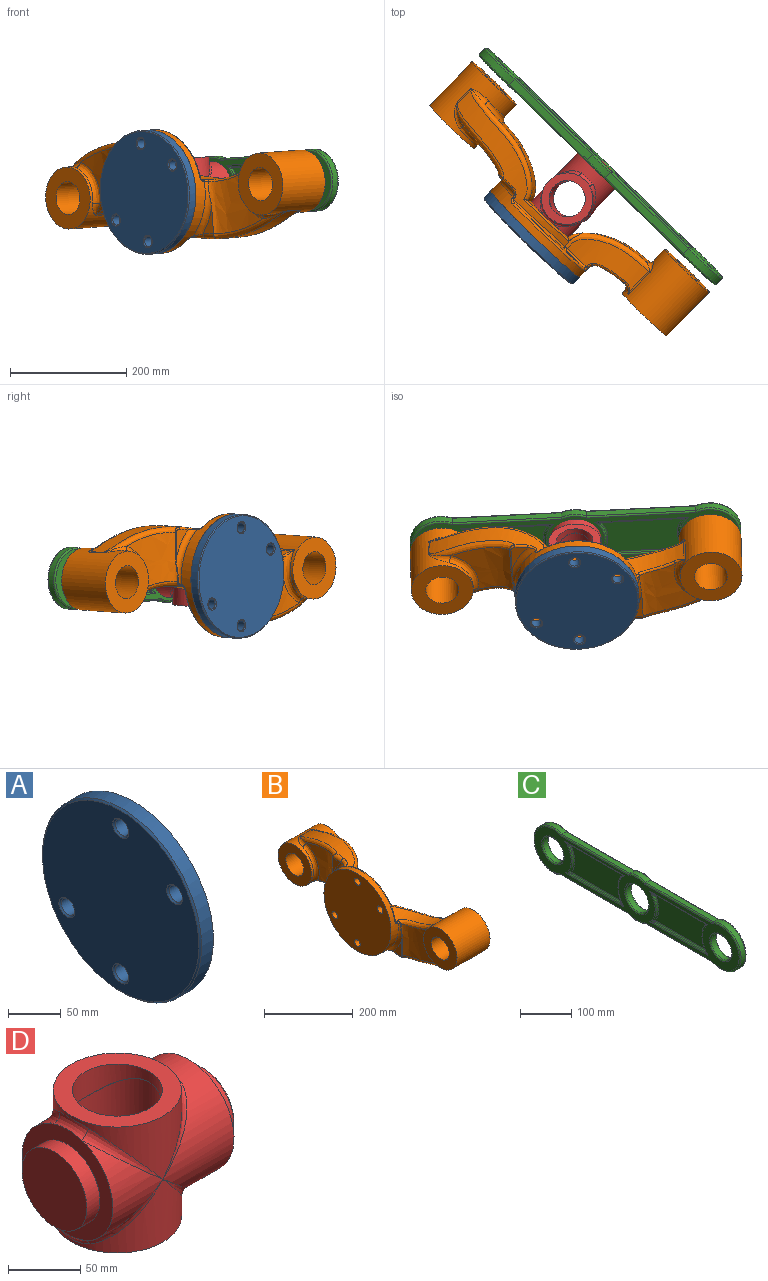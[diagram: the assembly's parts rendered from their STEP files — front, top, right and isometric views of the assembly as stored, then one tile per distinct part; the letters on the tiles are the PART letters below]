
ASSEMBLY  parts=4 mates=4
PART A: 12 faces, bbox 17.8x213.4x213.4 mm
  f0: cylinder r=8.89mm len=17.78mm, axis (1,0,0), area 893.8mm2, adj f6,f9
  f1: cylinder r=106.68mm len=213.36mm, axis (1,0,0), area 10726mm2, adj f6,f11
  f2: cylinder r=8.89mm len=17.78mm, axis (1,0,0), area 893.8mm2, adj f6,f10
  f3: cylinder r=8.89mm len=17.78mm, axis (1,0,0), area 893.8mm2, adj f6,f7
  f4: cylinder r=8.89mm len=17.78mm, axis (1,0,0), area 893.8mm2, adj f6,f8
  f5: plane 209.8x209.8mm, normal (-1,0,0), area 33141.3mm2, adj f7,f8,f9,f10,f11
  f6: plane 213.36x213.36mm, normal (1,0,0), area 34760.1mm2, adj f0,f1,f2,f3,f4
  f7: cone r=10.67mm half-angle=45deg, axis (-1,0,0), area 154.5mm2, adj f3,f5
  f8: cone r=10.67mm half-angle=45deg, axis (-1,0,0), area 154.5mm2, adj f4,f5
  f9: cone r=10.67mm half-angle=45deg, axis (-1,0,0), area 154.5mm2, adj f0,f5
  f10: cone r=8.89mm half-angle=45deg, axis (-1,0,0), area 154.5mm2, adj f2,f5
  f11: cone r=104.9mm half-angle=45deg, axis (1,0,0), area 1671.4mm2, adj f1,f5
PART B: 101 faces, bbox 139.1x569.9x231.1 mm
  f0: plane 151.16x93.4mm, normal (1,0,0), area 3907.4mm2, adj f7,f12,f25,f38,f78,f79,f80,f81
  f1: plane 106.68x106.68mm, normal (1,0,0), area 6395.9mm2, adj f2,f3
  f2: cylinder r=28.45mm len=104.9mm, axis (-1,0,0), area 18750.6mm2, adj f1,f4
  f3: cylinder r=53.34mm len=106.68mm, axis (-1,0,0), area 26347mm2, adj f1,f4,f40,f43,f44,f46,f47,f48
  f4: plane 106.68x106.68mm, normal (-1,0,0), area 6395.9mm2, adj f2,f3
  f5: cylinder r=256.25mm len=304.31mm, axis (-1,0,0), area 8276mm2, adj f25,f31,f32,f42,f58,f61,f62,f63
  f6: cylinder r=153.13mm len=128.87mm, axis (-1,0,0), area 4941.8mm2, adj f23,f29,f30,f67
  f7: extruded ~167.29x103.82mm, area 14672.5mm2, adj f0,f23,f24,f25,f78
  f8: extruded ~104.19x93.39mm, area 6218.3mm2, adj f29,f32,f35,f65,f66
  f9: cylinder r=256.25mm len=304.31mm, axis (-1,0,0), area 8055.6mm2, adj f23,f36,f38,f39,f41,f44,f45,f74
  f10: cylinder r=153.13mm len=128.87mm, axis (-1,0,0), area 5509.7mm2, adj f42,f48,f51,f52,f53,f54,f55
  f11: extruded ~104.21x99.66mm, area 7531.8mm2, adj f15,f37,f45,f49,f52
  f12: extruded ~167.29x103.82mm, area 14672.6mm2, adj f0,f38,f42,f43,f80
  f13: cylinder r=106.68mm len=213.36mm, axis (-1,0,0), area 11463.9mm2, adj f22,f26,f36,f37,f55,f57,f59,f60
  f14: plane 46.65x28.37mm, normal (-1,0,0), area 555.7mm2, adj f26,f63,f64,f65
  f15: plane 46.02x25.19mm, normal (-1,0,0), area 488.5mm2, adj f11,f37,f41,f45
  f16: cylinder r=53.34mm len=106.68mm, axis (-1,0,0), area 26286.9mm2, adj f17,f19,f24,f27,f28,f30,f31,f33
  f17: plane 106.68x106.68mm, normal (1,0,0), area 6395.9mm2, adj f16,f18
  f18: cylinder r=28.45mm len=104.9mm, axis (-1,0,0), area 18750.6mm2, adj f17,f19
  f19: plane 106.68x106.68mm, normal (-1,0,0), area 6395.9mm2, adj f16,f18
  f20: plane 158.94x84.9mm, normal (1,0,0), area 5064.9mm2, adj f54,f56,f58,f59,f86,f87
  f21: plane 158.94x84.9mm, normal (1,0,0), area 5064.9mm2, adj f67,f70,f71,f74,f77,f88,f89
  f22: plane 213.36x213.36mm, normal (-1,0,0), area 34760.1mm2, adj f13,f82,f83,f84,f85
  f23: bspline ~154.44x103.07mm, area 2156.6mm2, adj f6,f7,f9,f27,f70,f78
  f24: bspline ~80.73x49.33mm, area 1147.9mm2, adj f7,f16,f27,f28
  f25: bspline ~206.66x83.42mm, area 2956.7mm2, adj f0,f5,f7,f28,f81
  f26: torus R=115.57mm, axis (1,0,0), area 1170.8mm2, adj f13,f14,f62,f66,f68
  f27: bspline ~24.63x19.85mm, area 221.3mm2, adj f16,f23,f24,f30
  f28: bspline ~41.59x10.05mm, area 287.6mm2, adj f16,f24,f25,f31
  f29: bspline ~96.96x42.4mm, area 1170.7mm2, adj f6,f8,f33,f68,f71,f72
  f30: cylinder r=8.89mm len=34mm, axis (1,0,0), area 127.3mm2, adj f6,f16,f27,f33
  f31: cylinder r=8.89mm len=29.85mm, axis (-1,0,0), area 43.7mm2, adj f5,f16,f28,f34
  f32: bspline ~154.3x46.45mm, area 1853mm2, adj f5,f8,f34,f64
  f33: bspline ~25.18x21.29mm, area 258.9mm2, adj f16,f29,f30,f35
  f34: bspline ~40.91x32.76mm, area 353.1mm2, adj f16,f31,f32,f35
  f35: bspline ~79.04x51.99mm, area 1244mm2, adj f8,f16,f33,f34
  f36: cylinder r=8.89mm len=7.64mm, axis (1,0,0), area 14.5mm2, adj f9,f13,f39,f69
  f37: torus R=115.57mm, axis (1,0,0), area 1174.3mm2, adj f11,f13,f15,f39,f52,f53
  f38: bspline ~208.41x102.25mm, area 2956.9mm2, adj f0,f9,f12,f40,f79
  f39: bspline ~25.71x19.57mm, area 262.5mm2, adj f9,f36,f37,f41
  f40: bspline ~41.59x10.05mm, area 287.6mm2, adj f3,f38,f43,f44
  f41: torus R=247.36mm, axis (1,0,0), area 337.2mm2, adj f9,f15,f39,f45
  f42: bspline ~151.03x88.51mm, area 2157mm2, adj f5,f10,f12,f46,f56,f80
  f43: bspline ~78.14x49.61mm, area 1148mm2, adj f3,f12,f40,f46
  f44: cylinder r=8.89mm len=29.85mm, axis (-1,0,0), area 43.7mm2, adj f3,f9,f40,f47
  f45: bspline ~152.31x46.35mm, area 1821.1mm2, adj f9,f11,f15,f41,f47
  f46: bspline ~24.63x19.85mm, area 221.3mm2, adj f3,f42,f43,f48
  f47: bspline ~40.91x32.76mm, area 353.1mm2, adj f3,f44,f45,f49
  f48: cylinder r=8.89mm len=52.38mm, axis (1,0,0), area 186.1mm2, adj f3,f10,f46,f50
  f49: bspline ~100.99x50.99mm, area 1476.1mm2, adj f3,f11,f47,f50,f51
  f50: bspline ~5.35x3.86mm, area 5.1mm2, adj f48,f49,f51
  f51: bspline ~18.89x11.72mm, area 75.4mm2, adj f10,f49,f50,f52
  f52: bspline ~72.74x21.99mm, area 382.9mm2, adj f10,f11,f37,f51,f53
  f53: bspline ~11.85x6.97mm, area 42mm2, adj f10,f37,f52,f55
  f54: torus R=149.57mm, axis (-1,0,0), area 251.8mm2, adj f10,f20,f56,f57
  f55: cylinder r=3.56mm len=3.21mm, axis (-1,0,0), area 8.7mm2, adj f10,f13,f53,f57
  f56: torus R=12.45mm, axis (-1,0,0), area 31.3mm2, adj f20,f42,f54,f58
  f57: bspline ~8.68x8.6mm, area 41.5mm2, adj f13,f54,f55,f59
  f58: torus R=259.81mm, axis (-1,0,0), area 717.3mm2, adj f5,f20,f56,f60
  f59: torus R=103.12mm, axis (-1,0,0), area 1167.9mm2, adj f13,f20,f57,f60
  f60: bspline ~11x7.79mm, area 44.1mm2, adj f13,f58,f59,f61
  f61: cylinder r=3.56mm len=2.95mm, axis (1,0,0), area 5.6mm2, adj f5,f13,f60,f62
  f62: bspline ~16.84x14.77mm, area 82mm2, adj f5,f26,f61,f63
  f63: torus R=252.69mm, axis (1,0,0), area 119.6mm2, adj f5,f14,f62,f64
  f64: bspline ~12.14x10.45mm, area 48.7mm2, adj f14,f32,f63,f65
  f65: cylinder r=3.56mm len=41.47mm, axis (0,0,1), area 105.9mm2, adj f8,f14,f64,f66
  f66: bspline ~52.44x4.31mm, area 66.1mm2, adj f8,f26,f65,f68
  f67: torus R=149.57mm, axis (-1,0,0), area 245.4mm2, adj f6,f21,f70,f71
  f68: bspline ~8.07x7.71mm, area 26.8mm2, adj f26,f29,f66,f72
  f69: torus R=12.45mm, axis (-1,0,0), area 14.5mm2, adj f36,f73,f74
  f70: torus R=12.45mm, axis (-1,0,0), area 31.3mm2, adj f21,f23,f67,f74
  f71: bspline ~6.66x4.9mm, area 12.1mm2, adj f21,f29,f67,f75
  f72: bspline ~8.91x2.8mm, area 5.9mm2, adj f13,f29,f68,f75
  f73: bspline ~8.94x6.4mm, area 12.7mm2, adj f13,f69,f76
  f74: torus R=259.81mm, axis (-1,0,0), area 716.1mm2, adj f9,f21,f69,f70,f76
  f75: bspline ~8.92x8.52mm, area 39.3mm2, adj f13,f71,f72,f77
  f76: bspline ~8.96x5.35mm, area 23.3mm2, adj f13,f73,f74,f77
  f77: torus R=103.12mm, axis (-1,0,0), area 1167.9mm2, adj f13,f21,f75,f76
  f78: bspline ~32.54x19.35mm, area 166.3mm2, adj f0,f7,f9,f23,f79
  f79: torus R=252.69mm, axis (-1,0,0), area 627.5mm2, adj f0,f9,f38,f78
  f80: bspline ~34.18x19.94mm, area 166.2mm2, adj f0,f5,f12,f42,f81
  f81: torus R=252.69mm, axis (-1,0,0), area 627.5mm2, adj f0,f5,f25,f80
  f82: cylinder r=8.89mm len=17.78mm, axis (1,0,0), area 893.8mm2, adj f22,f88
  f83: cylinder r=8.89mm len=17.78mm, axis (1,0,0), area 893.8mm2, adj f22,f89
  f84: cylinder r=8.89mm len=17.78mm, axis (1,0,0), area 893.8mm2, adj f22,f86
  f85: cylinder r=8.89mm len=17.78mm, axis (1,0,0), area 893.8mm2, adj f22,f87
  f86: cone r=8.89mm half-angle=45deg, axis (1,0,0), area 154.5mm2, adj f20,f84
  f87: cone r=8.89mm half-angle=45deg, axis (1,0,0), area 154.5mm2, adj f20,f85
  f88: cone r=8.89mm half-angle=45deg, axis (1,0,0), area 154.5mm2, adj f21,f82
  f89: cone r=10.67mm half-angle=45deg, axis (1,0,0), area 154.5mm2, adj f21,f83
  f90: cylinder r=44.45mm len=84.3mm, axis (-1,0,0), area 11.6mm2, adj f0,f92,f97,f98
  f91: cylinder r=44.45mm len=84.3mm, axis (-1,0,0), area 11.6mm2, adj f0,f94,f95,f98
  f92: bspline ~0.3x0.21mm, area 0mm2, adj f0,f90,f93
  f93: bspline ~30.61x9.54mm, area 3.1mm2, adj f0,f92,f94,f98
  f94: bspline ~0.3x0.21mm, area 0mm2, adj f0,f91,f93
  f95: bspline ~0.3x0.21mm, area 0mm2, adj f0,f91,f96
  f96: bspline ~30.61x9.54mm, area 3.1mm2, adj f0,f95,f97,f98
  f97: bspline ~0.3x0.21mm, area 0mm2, adj f0,f90,f96
  f98: plane 88.9x88.9mm, normal (1,0,0), area 2513.3mm2, adj f90,f91,f93,f96,f99
  f99: cylinder r=34.29mm len=68.58mm, axis (1,0,0), area 2736.2mm2, adj f98,f100
  f100: plane 68.58x68.58mm, normal (1,0,0), area 3693.9mm2, adj f99
PART C: 103 faces, bbox 17.8x578.5x115.5 mm
  f0: plane 187.19x12.45mm, normal (0,0,-1), area 2329.8mm2, adj f1,f10,f21,f40
  f1: cylinder r=53.34mm len=106.68mm, axis (-1,0,0), area 2654.3mm2, adj f0,f2,f19,f38
  f2: plane 187.19x12.45mm, normal (0,0,1), area 2329.8mm2, adj f1,f3,f17,f36
  f3: cylinder r=53.34mm len=44.31mm, axis (-1,0,0), area 568.7mm2, adj f2,f4,f18,f37
  f4: plane 187.19x12.45mm, normal (0,0,1), area 2329.8mm2, adj f3,f5,f20,f39
  f5: cylinder r=53.34mm len=106.68mm, axis (-1,0,0), area 2654.3mm2, adj f4,f6,f22,f41
  f6: plane 187.19x12.45mm, normal (0,0,-1), area 2329.8mm2, adj f5,f10,f24,f43
  f7: cylinder r=28.45mm len=56.9mm, axis (-1,0,0), area 2224.6mm2, adj f29,f48
  f8: cylinder r=31.2mm len=62.41mm, axis (-1,0,0), area 2440.2mm2, adj f30,f49
  f9: cylinder r=28.45mm len=56.9mm, axis (-1,0,0), area 2224.6mm2, adj f31,f50
  f10: cylinder r=53.34mm len=44.31mm, axis (-1,0,0), area 568.7mm2, adj f0,f6,f23,f42
  f11: plane 564.34x101.35mm, normal (1,0,0), area 20769.7mm2, adj f36,f37,f38,f39,f40,f41,f42,f43
  f12: plane 564.34x101.35mm, normal (-1,0,0), area 20769.7mm2, adj f17,f18,f19,f20,f21,f22,f23,f24
  f13: plane 138.43x62.06mm, normal (-1,0,0), area 7799.5mm2, adj f55,f56,f57,f58
  f14: plane 138.43x62.06mm, normal (1,0,0), area 7799.5mm2, adj f59,f60,f61,f62
  f15: plane 141.52x64.26mm, normal (-1,0,0), area 8107.3mm2, adj f63,f64,f65,f66
  f16: plane 141.52x64.26mm, normal (1,0,0), area 8107.3mm2, adj f67,f68,f69,f70
  f17: cylinder r=2.67mm len=188.36mm, axis (0,-1,0), area 786.7mm2, adj f2,f12,f18,f19
  f18: torus R=50.67mm, axis (1,0,0), area 190.4mm2, adj f3,f12,f17,f20
  f19: torus R=50.67mm, axis (1,0,0), area 879.7mm2, adj f1,f12,f17,f21
  f20: cylinder r=2.67mm len=188.36mm, axis (0,-1,0), area 786.7mm2, adj f4,f12,f18,f22
  f21: cylinder r=2.67mm len=188.36mm, axis (0,1,0), area 786.7mm2, adj f0,f12,f19,f23
  f22: torus R=50.67mm, axis (1,0,0), area 879.7mm2, adj f5,f12,f20,f24
  f23: torus R=50.67mm, axis (1,0,0), area 190.4mm2, adj f10,f12,f21,f24
  f24: cylinder r=2.67mm len=188.36mm, axis (0,1,0), area 786.7mm2, adj f6,f12,f22,f23
  f25: torus R=50.67mm, axis (1,0,0), area 270.6mm2, adj f12,f63,f80,f82
  f26: cylinder r=2.67mm len=165.58mm, axis (0,1,0), area 563.4mm2, adj f12,f64,f80,f84
  f27: cylinder r=2.67mm len=160.77mm, axis (0,-1,0), area 549.7mm2, adj f12,f65,f82,f86
  f28: torus R=50.67mm, axis (1,0,0), area 270.6mm2, adj f12,f66,f84,f86
  f29: torus R=31.12mm, axis (1,0,0), area 774.3mm2, adj f7,f12
  f30: torus R=33.87mm, axis (1,0,0), area 846.9mm2, adj f8,f12
  f31: torus R=31.12mm, axis (1,0,0), area 774.3mm2, adj f9,f12
  f32: torus R=50.67mm, axis (1,0,0), area 260.2mm2, adj f12,f56,f96,f100
  f33: cylinder r=2.67mm len=160.77mm, axis (0,-1,0), area 549.7mm2, adj f12,f55,f96,f98
  f34: cylinder r=2.67mm len=160.77mm, axis (0,1,0), area 549.7mm2, adj f12,f58,f100,f102
  f35: torus R=50.67mm, axis (1,0,0), area 260.2mm2, adj f12,f57,f98,f102
  f36: cylinder r=2.67mm len=188.36mm, axis (0,1,0), area 786.7mm2, adj f2,f11,f37,f38
  f37: torus R=50.67mm, axis (1,0,0), area 190.4mm2, adj f3,f11,f36,f39
  f38: torus R=50.67mm, axis (1,0,0), area 879.7mm2, adj f1,f11,f36,f40
  f39: cylinder r=2.67mm len=188.36mm, axis (0,1,0), area 786.7mm2, adj f4,f11,f37,f41
  f40: cylinder r=2.67mm len=188.36mm, axis (0,-1,0), area 786.7mm2, adj f0,f11,f38,f42
  f41: torus R=50.67mm, axis (1,0,0), area 879.7mm2, adj f5,f11,f39,f43
  f42: torus R=50.67mm, axis (1,0,0), area 190.4mm2, adj f10,f11,f40,f43
  f43: cylinder r=2.67mm len=188.36mm, axis (0,-1,0), area 786.7mm2, adj f6,f11,f41,f42
  f44: torus R=50.67mm, axis (1,0,0), area 270.6mm2, adj f11,f67,f72,f74
  f45: cylinder r=2.67mm len=165.58mm, axis (0,-1,0), area 563.4mm2, adj f11,f68,f72,f76
  f46: cylinder r=2.67mm len=160.77mm, axis (0,1,0), area 549.7mm2, adj f11,f69,f74,f78
  f47: torus R=50.67mm, axis (1,0,0), area 270.6mm2, adj f11,f70,f76,f78
  f48: torus R=31.12mm, axis (1,0,0), area 774.3mm2, adj f7,f11
  f49: torus R=33.87mm, axis (1,0,0), area 846.9mm2, adj f8,f11
  f50: torus R=31.12mm, axis (1,0,0), area 774.3mm2, adj f9,f11
  f51: torus R=50.67mm, axis (1,0,0), area 260.2mm2, adj f11,f60,f88,f92
  f52: cylinder r=2.67mm len=160.77mm, axis (0,1,0), area 549.7mm2, adj f11,f59,f88,f90
  f53: cylinder r=2.67mm len=160.77mm, axis (0,-1,0), area 549.7mm2, adj f11,f62,f92,f94
  f54: torus R=50.67mm, axis (1,0,0), area 260.2mm2, adj f11,f61,f90,f94
  f55: cylinder r=2.67mm len=138.43mm, axis (0,-1,0), area 518.1mm2, adj f13,f33,f95,f97
  f56: torus R=55.93mm, axis (1,0,0), area 239.3mm2, adj f13,f32,f95,f99
  f57: torus R=55.93mm, axis (1,0,0), area 239.3mm2, adj f13,f35,f97,f101
  f58: cylinder r=2.67mm len=138.43mm, axis (0,1,0), area 518.1mm2, adj f13,f34,f99,f101
  f59: cylinder r=2.67mm len=138.43mm, axis (0,1,0), area 518.1mm2, adj f14,f52,f87,f89
  f60: torus R=55.93mm, axis (1,0,0), area 239.3mm2, adj f14,f51,f87,f91
  f61: torus R=55.93mm, axis (1,0,0), area 239.3mm2, adj f14,f54,f89,f93
  f62: cylinder r=2.67mm len=138.43mm, axis (0,-1,0), area 518.1mm2, adj f14,f53,f91,f93
  f63: torus R=55.93mm, axis (1,0,0), area 249mm2, adj f15,f25,f79,f81
  f64: cylinder r=2.67mm len=141.52mm, axis (0,1,0), area 529.7mm2, adj f15,f26,f79,f83
  f65: cylinder r=2.67mm len=138.43mm, axis (0,-1,0), area 518.1mm2, adj f15,f27,f81,f85
  f66: torus R=55.93mm, axis (1,0,0), area 249mm2, adj f15,f28,f83,f85
  f67: torus R=55.93mm, axis (1,0,0), area 249mm2, adj f16,f44,f71,f73
  f68: cylinder r=2.67mm len=141.52mm, axis (0,-1,0), area 529.7mm2, adj f16,f45,f71,f75
  f69: cylinder r=2.67mm len=138.43mm, axis (0,1,0), area 518.1mm2, adj f16,f46,f73,f77
  f70: torus R=55.93mm, axis (1,0,0), area 249mm2, adj f16,f47,f75,f77
  f71: sphere r=2.67mm, area 10.5mm2, adj f67,f68,f72
  f72: bspline ~12.08x6.85mm, area 27.7mm2, adj f44,f45,f71
  f73: sphere r=2.67mm, area 10.4mm2, adj f67,f69,f74
  f74: bspline ~11.21x6.74mm, area 25.7mm2, adj f44,f46,f73
  f75: sphere r=2.67mm, area 10.5mm2, adj f68,f70,f76
  f76: bspline ~12.08x6.85mm, area 27.7mm2, adj f45,f47,f75
  f77: sphere r=2.67mm, area 10.4mm2, adj f69,f70,f78
  f78: bspline ~11.21x6.74mm, area 25.7mm2, adj f46,f47,f77
  f79: sphere r=2.67mm, area 11.2mm2, adj f63,f64,f80
  f80: bspline ~12.08x6.85mm, area 27.7mm2, adj f25,f26,f79
  f81: sphere r=2.67mm, area 11.1mm2, adj f63,f65,f82
  f82: bspline ~11.21x6.74mm, area 25.7mm2, adj f25,f27,f81
  f83: sphere r=2.67mm, area 10.5mm2, adj f64,f66,f84
  f84: bspline ~12.08x6.85mm, area 27.7mm2, adj f26,f28,f83
  f85: sphere r=2.67mm, area 10.4mm2, adj f65,f66,f86
  f86: bspline ~11.21x6.74mm, area 25.7mm2, adj f27,f28,f85
  f87: sphere r=2.67mm, area 10.4mm2, adj f59,f60,f88
  f88: bspline ~11.21x6.74mm, area 25.7mm2, adj f51,f52,f87
  f89: sphere r=2.67mm, area 10.4mm2, adj f59,f61,f90
  f90: bspline ~11.21x6.74mm, area 25.7mm2, adj f52,f54,f89
  f91: sphere r=2.67mm, area 10.4mm2, adj f60,f62,f92
  f92: bspline ~11.21x6.74mm, area 25.7mm2, adj f51,f53,f91
  f93: sphere r=2.67mm, area 10.4mm2, adj f61,f62,f94
  f94: bspline ~11.21x6.74mm, area 25.7mm2, adj f53,f54,f93
  f95: sphere r=2.67mm, area 10.4mm2, adj f55,f56,f96
  f96: bspline ~11.21x6.74mm, area 25.7mm2, adj f32,f33,f95
  f97: sphere r=2.67mm, area 11.1mm2, adj f55,f57,f98
  f98: bspline ~11.21x6.74mm, area 25.7mm2, adj f33,f35,f97
  f99: sphere r=2.67mm, area 10.4mm2, adj f56,f58,f100
  f100: bspline ~11.21x6.74mm, area 25.7mm2, adj f32,f34,f99
  f101: sphere r=2.67mm, area 11.1mm2, adj f57,f58,f102
  f102: bspline ~11.21x6.74mm, area 25.7mm2, adj f34,f35,f101
PART D: 31 faces, bbox 146.3x89.1x106.9 mm
  f0: cylinder r=44.45mm len=84.3mm, axis (-1,0,0), area 2295mm2, adj f4,f16,f24
  f1: cylinder r=31.2mm len=62.41mm, axis (0,0,-1), area 2943.6mm2, adj f3,f11
  f2: cylinder r=44.45mm len=88.9mm, axis (0,0,-1), area 5745.3mm2, adj f3,f16,f17,f18,f19,f20,f21
  f3: plane 88.9x88.9mm, normal (0,0,1), area 3148.3mm2, adj f1,f2
  f4: plane 89.1x89.1mm, normal (-1,0,0), area 3040.2mm2, adj f0,f5,f17,f23,f29
  f5: cylinder r=44.45mm len=84.3mm, axis (-1,0,0), area 2295mm2, adj f4,f18,f22
  f6: cylinder r=31.2mm len=62.41mm, axis (0,0,-1), area 2944mm2, adj f7,f10
  f7: plane 88.9x88.9mm, normal (0,0,-1), area 3148.3mm2, adj f6,f8
  f8: cylinder r=44.45mm len=88.9mm, axis (0,0,-1), area 5745.3mm2, adj f7,f13,f14,f15,f22,f23,f24
  f9: cylinder r=44.45mm len=88.9mm, axis (-1,0,0), area 10399.9mm2, adj f13,f14,f15,f19,f20,f21,f25
  f10: cylinder r=44.45mm len=62.41mm, axis (-1,0,0), area 22.6mm2, adj f6,f12
  f11: cylinder r=44.45mm len=62.41mm, axis (-1,0,0), area 22.6mm2, adj f1,f12
  f12: cylinder r=31.12mm len=88.9mm, axis (0,0,1), area 15000mm2, adj f10,f11
  f13: bspline ~49.83x49.83mm, area 400.8mm2, adj f8,f9,f14
  f14: bspline ~30.61x9.54mm, area 254.5mm2, adj f8,f9,f13,f15
  f15: bspline ~49.83x49.83mm, area 397.4mm2, adj f8,f9,f14
  f16: bspline ~49.83x49.83mm, area 400.8mm2, adj f0,f2,f17
  f17: bspline ~30.61x9.54mm, area 254.5mm2, adj f2,f4,f16,f18
  f18: bspline ~49.83x49.83mm, area 400.8mm2, adj f2,f5,f17
  f19: bspline ~49.83x49.83mm, area 400.8mm2, adj f2,f9,f20
  f20: bspline ~30.61x9.54mm, area 254.5mm2, adj f2,f9,f19,f21
  f21: bspline ~49.83x49.83mm, area 400.8mm2, adj f2,f9,f20
  f22: bspline ~49.83x49.83mm, area 383.8mm2, adj f5,f8,f23
  f23: bspline ~30.61x9.54mm, area 254.5mm2, adj f4,f8,f22,f24
  f24: bspline ~49.83x49.83mm, area 400.8mm2, adj f0,f8,f23
  f25: plane 88.9x88.9mm, normal (1,0,0), area 3165.7mm2, adj f9,f28
  f26: plane 58.67x58.67mm, normal (1,0,0), area 2703.8mm2, adj f27
  f27: cone r=29.34mm half-angle=45deg, axis (-1,0,0), area 477.5mm2, adj f26,f28
  f28: cylinder r=31.12mm len=62.23mm, axis (-1,0,0), area 2537.5mm2, adj f25,f27
  f29: cylinder r=31.75mm len=63.5mm, axis (1,0,0), area 2533.5mm2, adj f4,f30
  f30: plane 63.5x63.5mm, normal (-1,0,0), area 3166.9mm2, adj f29
PLACE A rot(axis=(0.92,0.39,0.03),178.4deg) t=(-64.25,0,26.71)mm
PLACE B rot(axis=(0.92,0.39,0.03),178.4deg) t=(-64.25,0,26.71)mm
PLACE C rot(axis=(0.92,0.39,0.03),178.4deg) t=(-65.16,-0.94,26.64)mm
PLACE D rot(axis=(0.92,0.39,0.03),178.4deg) t=(-64.25,0,26.71)mm fixed
MATE fastened A.f1 <-> B.f13  axis (0.69,0.72,0.05) through (-122.92,-60.6,22.44)mm
MATE revolute C.f8 <-> D.f0  axis (0.69,0.72,0.05) through (-15.83,50.01,30.22)mm
MATE revolute D.f29 <-> B.f99  axis (-0.69,-0.72,-0.05) through (-107.04,-44.2,23.6)mm
MATE cylindrical B.f16 <-> C.f5  axis (0.69,0.72,0.05) through (-193.5,198.87,17.31)mm
